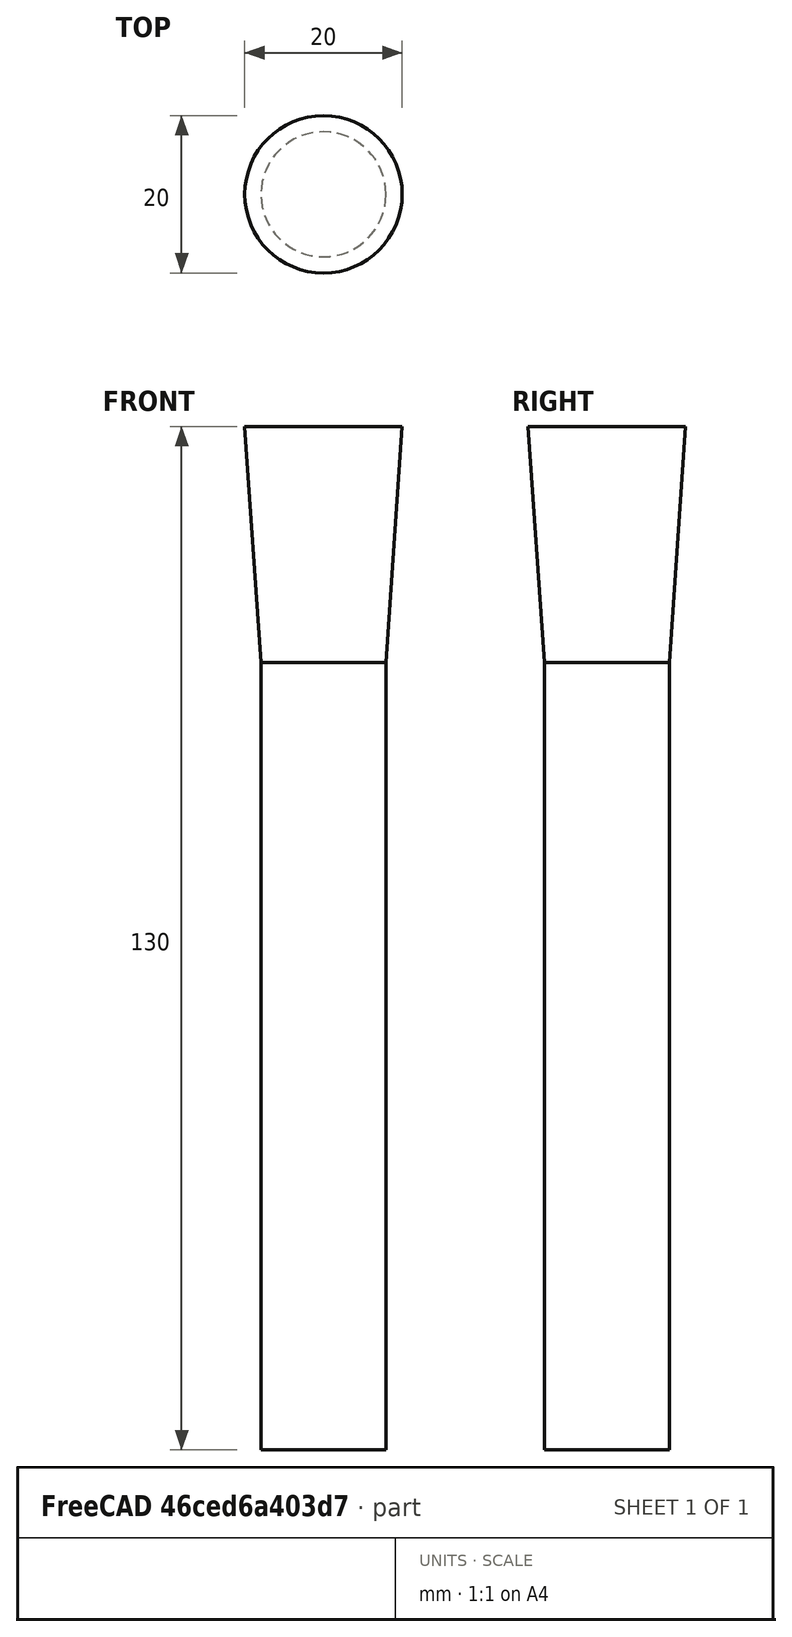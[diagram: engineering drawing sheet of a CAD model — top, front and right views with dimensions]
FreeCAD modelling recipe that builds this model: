
FCSTD DOCUMENT  (FreeCAD 0.19R24291 (Git))
Label: marker
License: All rights reserved
LicenseURL: http://en.wikipedia.org/wiki/All_rights_reserved
objects: Sketcher::SketchObject×1, PartDesign::Revolution×1, PartDesign::Body×1
note: 4 computed .brp shape members not serialized (recipe doc carries the construction recipe); baked Part::Feature solids carry a one-line shape summary decoded from their .brp

FEATURE [Sketcher::SketchObject] Sketch
  FullyConstrained = true
  MapMode = 5
  Placement = pos=(0,0,0) rot=(1,0,0;1.5708rad)
  Support = -> [XZ_Plane]
  expr: Constraints[8] = 5 / 8 * 25.4 / 2
  expr: Constraints[10] = 20 / 2
  sketch-geometry (5):
    g0: LineSegment StartX=0 StartY=0 StartZ=0 EndX=-7.9375 EndY=0 EndZ=0
    g1: LineSegment StartX=-7.9375 StartY=100 StartZ=0 EndX=-7.9375 EndY=0 EndZ=0
    g2: LineSegment StartX=-7.9375 StartY=100 StartZ=0 EndX=-10 EndY=130 EndZ=0
    g3: LineSegment StartX=-10 StartY=130 StartZ=0 EndX=0 EndY=130 EndZ=0
    g4: LineSegment StartX=0 StartY=130 StartZ=0 EndX=0 EndY=0 EndZ=0
  constraints (14):
    c: Coincident(g0,g-1)
    c: Horizontal(g0)
    c: Vertical(g1)
    c: Coincident(g2,g1)
    c: Horizontal(g3)
    c: Coincident(g4,g3)
    c: Vertical(g4)
    c: Coincident(g4,g0)
    c: DistanceX(g0,g0) = 7.9375
    c: Coincident(g1,g0)
    c: DistanceX(g3,g3) = 10
    c: Coincident(g2,g3)
    c: DistanceY(g0,g1) = 100
    c: DistanceY(g1,g2) = 30
FEATURE [PartDesign::Revolution] Revolution
  Angle = 360
  Axis = (0,2e-16,1)
  Base = (0,0,0)
  Placement = pos=(0,0,0) rot=(1,0,0;1.5708rad)
  Profile = -> Sketch
  ReferenceAxis = -> Sketch [V_Axis]
FEATURE [PartDesign::Body] Body
  Group = -> [Sketch,Revolution]
  Origin = -> Origin
  Tip = -> Revolution
